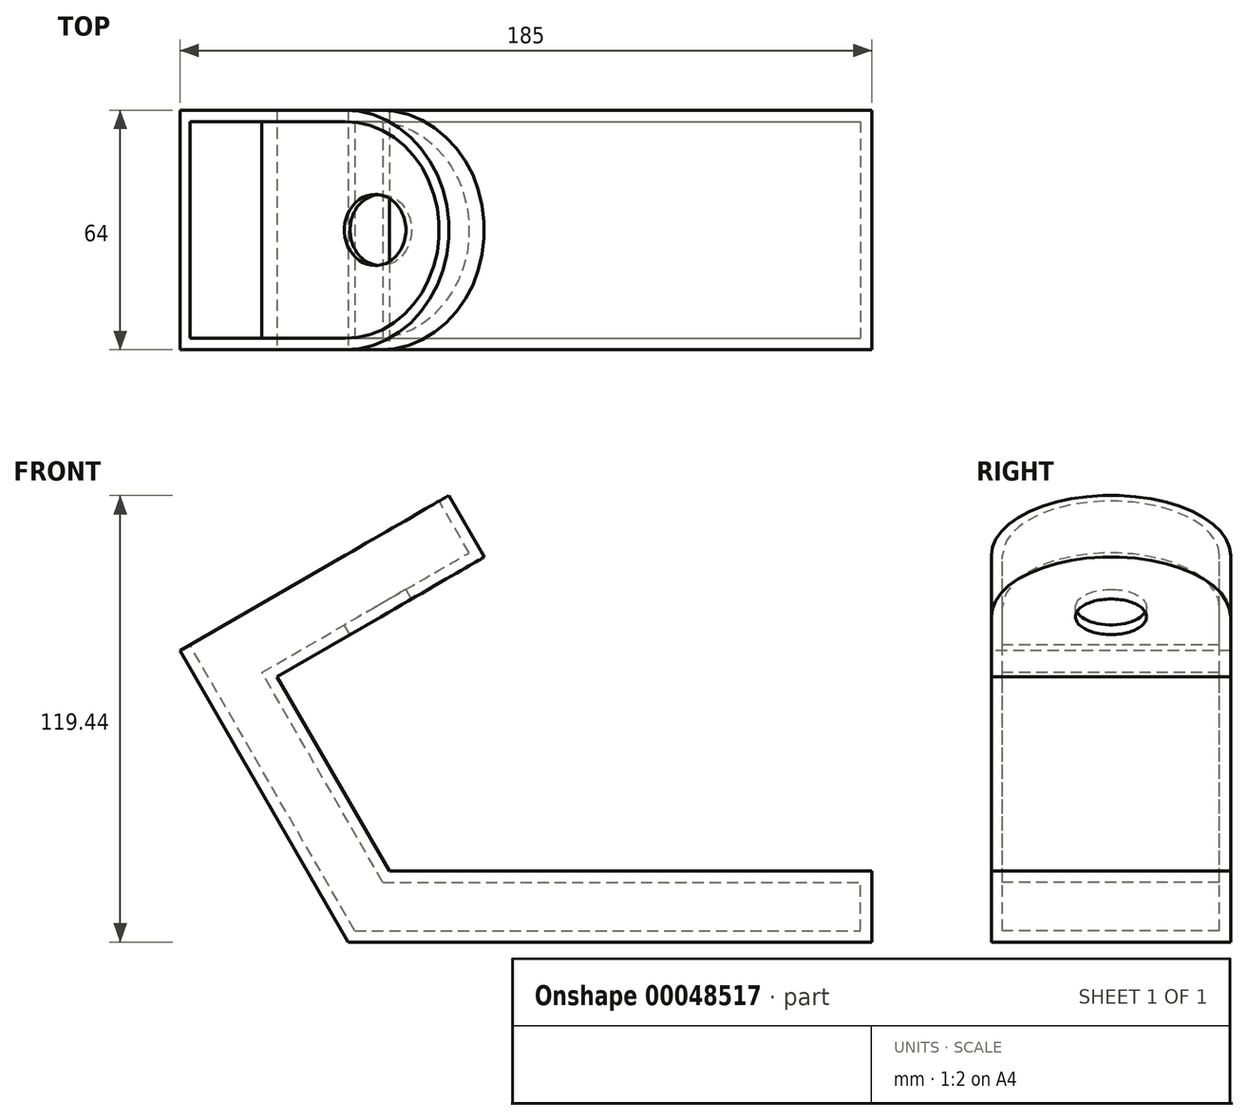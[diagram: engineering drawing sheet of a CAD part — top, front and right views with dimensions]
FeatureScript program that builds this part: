
annotation { "Feature Type Name" : "Feature", "Feature Type Description" : "" }
export const myFeature = defineFeature(function(context is Context, id is Id, definition is map)
    precondition{}
    {
        {
            var Q0;
            Q0=qCreatedBy(makeId("Front.planeOp"),FACE);
            var sketch = newSketch(context, id + "F0", { "sketchPlane" : qUnion([Q0])});
            skLineSegment(sketch, "E0", {"start": v(0, 0) * mm, "end": v(-45, 77.94) * mm});
            skLineSegment(sketch, "E1", {"start": v(-45, 77.94) * mm, "end": v(26.88, 119.44) * mm});
            skLineSegment(sketch, "E2", {"start": v(0, 0) * mm, "end": v(140, 0) * mm});
            skLineSegment(sketch, "E3.1", {"start": v(10.97, 19) * mm, "end": v(-19.05, 70.99) * mm});
            skLineSegment(sketch, "E4", {"start": v(-19.05, 70.99) * mm, "end": v(36.38, 102.99) * mm});
            skLineSegment(sketch, "E5", {"start": v(10.97, 19) * mm, "end": v(140, 19) * mm});
            skLineSegment(sketch, "E6", {"start": v(140, 0) * mm, "end": v(140, 19) * mm});
            skLineSegment(sketch, "E7", {"start": v(26.88, 119.44) * mm, "end": v(36.38, 102.99) * mm});
            skSolve(sketch);
        }
        {
            var Q0;
            Q0 = qSketchRegion(id + "F0", true);
            extrude(context, id + "F1", {"entities" : qUnion([Q0]), "oppositeDirection" : true, "depth" : 64 * mm});
        }
        {
            var Q0;
            Q0=makeQuery(id+"F1.opExtrude","SWEPT_FACE",FACE,{"disambiguationData":[OSD([sQuery(id+"F0.wireOp",EDGE,"E1")])]});
            var sketch = newSketch(context, id + "F2", { "sketchPlane" : qUnion([Q0])});
            skCircle(sketch, "E8", {"center": v(51, 32) * mm, "radius": 32 * mm});
            skPoint(sketch, "E8.centerSnap0", {"position": v(83, 32) * mm});
            skSolve(sketch);
        }
        {
            var Q0;
            {var subQ0=sQuery(id+"F0.wireOp",EDGE,"E1");var subQ1=makeQuery(id+"F1.opExtrude","CAP_EDGE",EDGE,{"disambiguationData":[OSD([subQ0])],"isStart":false});var subQ2=sQuery(id+"F2.wireOp",EDGE,"E8");var subQ3=makeQuery(id+"F2.imprint","INTERSECT",VERTEX,{"derivedFrom":[subQ1,subQ2]});Q0=makeQuery(id+"F2.imprint","IMPRINT",FACE,{"disambiguationData":[TD([[makeQuery(id+"F2.imprint","IMPRINT",EDGE,{"disambiguationData":[TD([[subQ3,1.0]])],"derivedFrom":subQ2}),-1.0]])]});}
            var Q1;
            {var subQ0=sQuery(id+"F0.wireOp",EDGE,"E1");var subQ1=makeQuery(id+"F1.opExtrude","CAP_EDGE",EDGE,{"disambiguationData":[OSD([subQ0])],"isStart":true});var subQ2=sQuery(id+"F2.wireOp",EDGE,"E8");var subQ3=makeQuery(id+"F2.imprint","INTERSECT",VERTEX,{"derivedFrom":[subQ1,subQ2]});Q1=makeQuery(id+"F2.imprint","IMPRINT",FACE,{"disambiguationData":[TD([[makeQuery(id+"F2.imprint","IMPRINT",EDGE,{"disambiguationData":[TD([[subQ3,-1.0]])],"derivedFrom":subQ2}),-1.0]])]});}
            extrude(context, id + "F3", {"entities" : qUnion([Q0, Q1]), "operationType" : NewBodyOperationType.REMOVE, "oppositeDirection" : true, "depth" : 25 * mm});
        }
        {
            var Q0;
            Q0=makeQuery(id+"F1.opExtrude","SWEPT_FACE",FACE,{"disambiguationData":[OSD([sQuery(id+"F0.wireOp",EDGE,"E1")])]});
            shell(context, id + "F4", {"entities" : qUnion([Q0]), "thickness" : 3 * mm});
        }
        {
            var Q0;
            Q0=makeQuery(id+"F4.opShell","OFFSET_FACE",FACE,{"disambiguationData":[OSD([sQuery(id+"F0.wireOp",EDGE,"E4")])]});
            var sketch = newSketch(context, id + "F5", { "sketchPlane" : qUnion([Q0])});
            skCircle(sketch, "E9", {"center": v(51, 32) * mm, "radius": 9.5 * mm});
            skSolve(sketch);
        }
        {
            var Q0;
            Q0 = qSketchRegion(id + "F5", true);
            var Q1;
            Q1=makeQuery(id+"F1.opExtrude","SWEPT_FACE",FACE,{"disambiguationData":[OSD([sQuery(id+"F0.wireOp",EDGE,"E4")])]});
            extrude(context, id + "F6", {"entities" : qUnion([Q0]), "operationType" : NewBodyOperationType.REMOVE, "endBound" : BoundingType.UP_TO_SURFACE, "oppositeDirection" : true, "endBoundEntityFace" : qUnion([Q1]), "depth" : 25 * mm});
        }
    });
